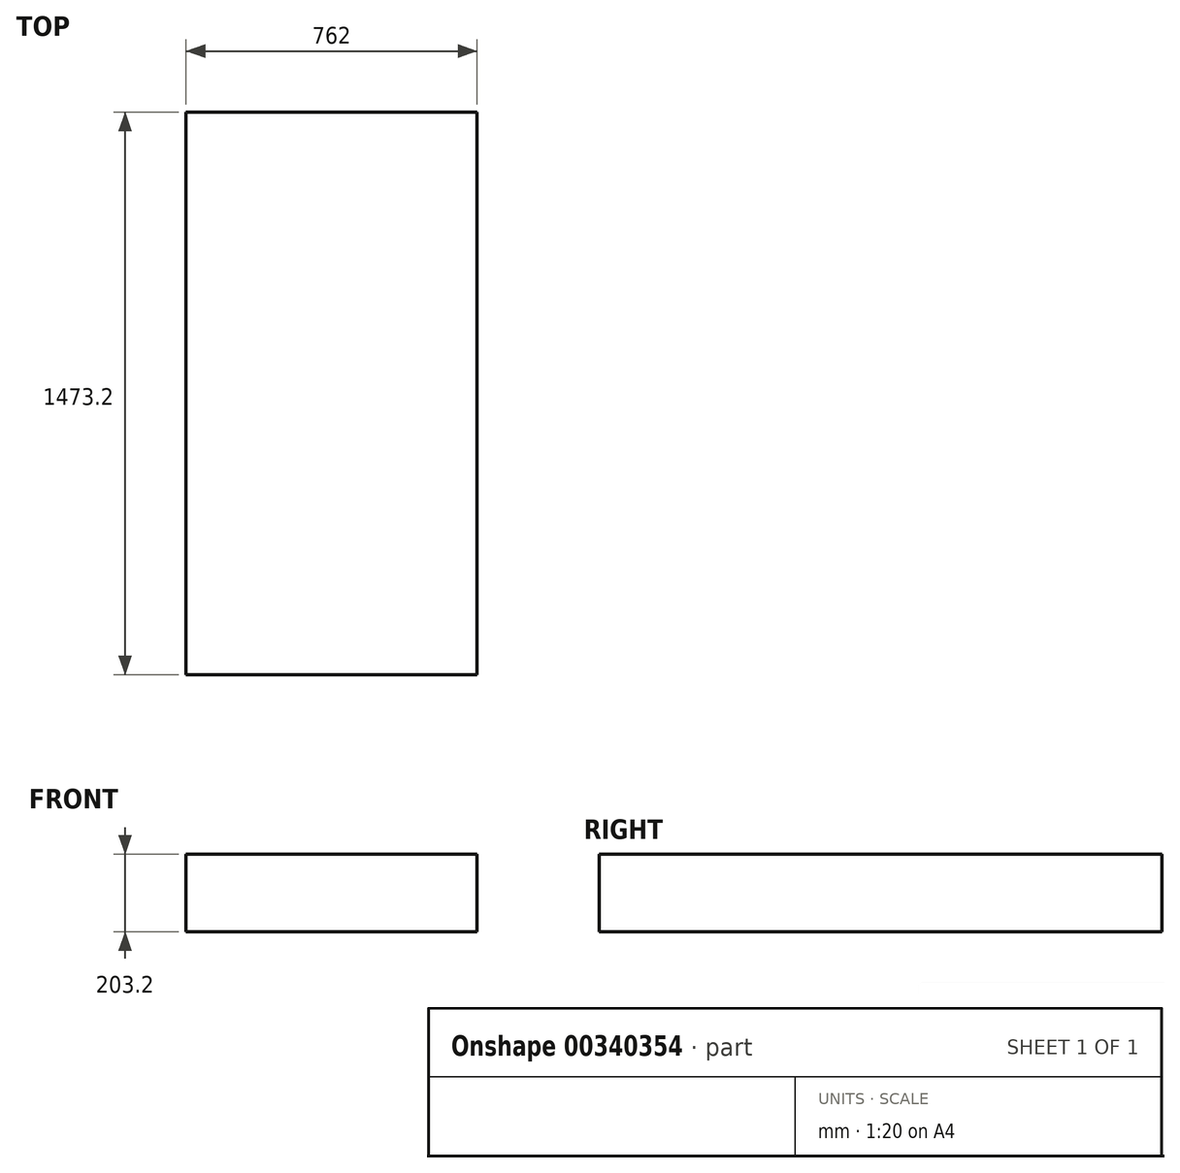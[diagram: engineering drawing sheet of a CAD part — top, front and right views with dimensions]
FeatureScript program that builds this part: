
annotation { "Feature Type Name" : "Feature", "Feature Type Description" : "" }
export const myFeature = defineFeature(function(context is Context, id is Id, definition is map)
    precondition{}
    {
        {
            var Q0;
            Q0=qCreatedBy(makeId("Front.planeOp"),FACE);
            var sketch = newSketch(context, id + "F0", { "sketchPlane" : qUnion([Q0])});
            skLineSegment(sketch, "E0.bottom", {"start": v(0, 22.39) * mm, "end": v(-762, 22.39) * mm});
            skLineSegment(sketch, "E0.top", {"start": v(0, 225.59) * mm, "end": v(-762, 225.59) * mm});
            skLineSegment(sketch, "E0.left", {"start": v(0, 22.39) * mm, "end": v(0, 225.59) * mm});
            skLineSegment(sketch, "E0.right", {"start": v(-762, 22.39) * mm, "end": v(-762, 225.59) * mm});
            skSolve(sketch);
        }
        {
            var Q0;
            Q0=makeQuery(id+"F0.imprint","IMPRINT",FACE,{"disambiguationData":[TD([[makeQuery(id+"F0.imprint","IMPRINT",EDGE,{"derivedFrom":sQuery(id+"F0.wireOp",EDGE,"E0.bottom")}),-1.0]])]});
            extrude(context, id + "F1", {"entities" : qUnion([Q0]), "depth" : 1473.2 * mm});
        }
    });
